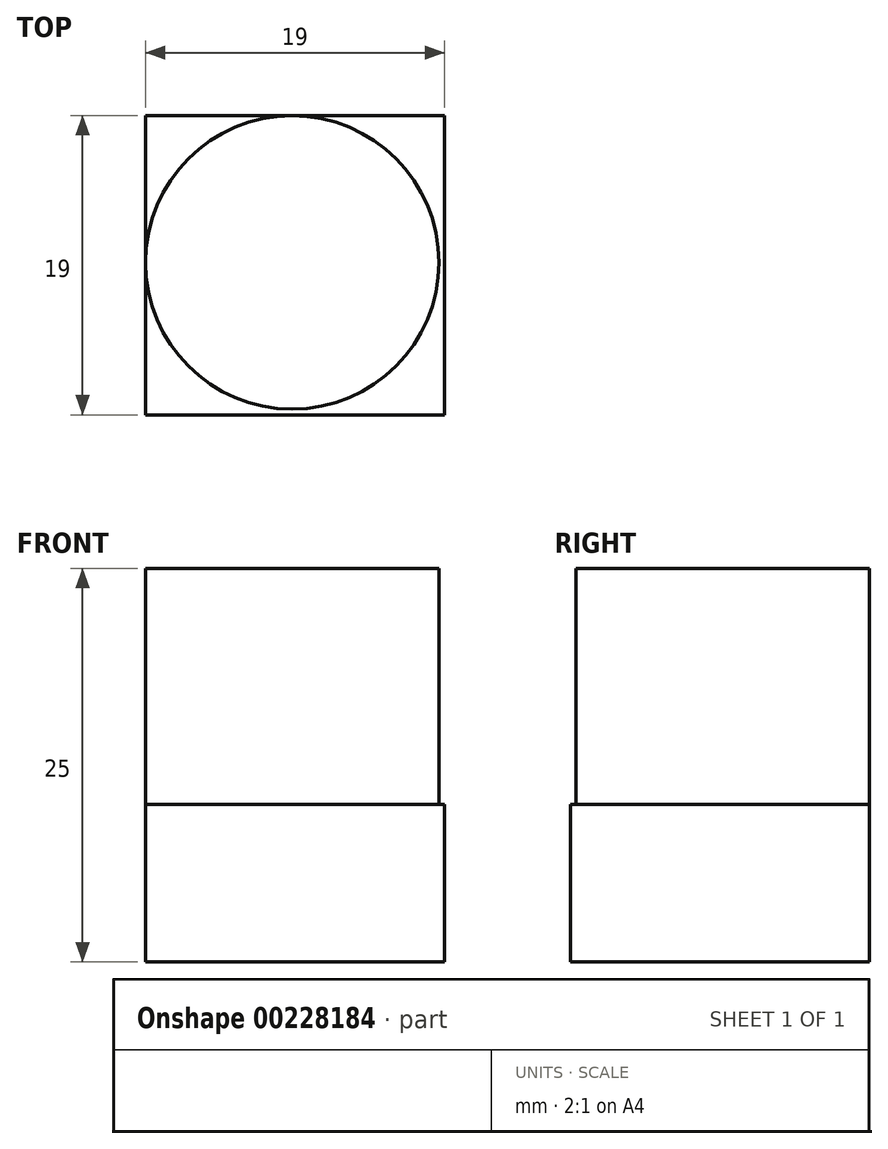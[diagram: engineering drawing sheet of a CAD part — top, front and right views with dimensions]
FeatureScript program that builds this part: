
annotation { "Feature Type Name" : "Feature", "Feature Type Description" : "" }
export const myFeature = defineFeature(function(context is Context, id is Id, definition is map)
    precondition{}
    {
        {
            var Q0;
            Q0=qCreatedBy(makeId("Top.planeOp"),FACE);
            var sketch = newSketch(context, id + "F0", { "sketchPlane" : qUnion([Q0])});
            skLineSegment(sketch, "E0.bottom", {"start": v(-9.32, 5.92) * mm, "end": v(9.68, 5.92) * mm});
            skLineSegment(sketch, "E0.top", {"start": v(-9.32, -13.08) * mm, "end": v(9.68, -13.08) * mm});
            skLineSegment(sketch, "E0.left", {"start": v(-9.32, 5.92) * mm, "end": v(-9.32, -13.08) * mm});
            skLineSegment(sketch, "E0.right", {"start": v(9.68, 5.92) * mm, "end": v(9.68, -13.08) * mm});
            skSolve(sketch);
        }
        {
            var Q0;
            Q0 = qSketchRegion(id + "F0", true);
            extrude(context, id + "F1", {"entities" : qUnion([Q0]), "depth" : 10 * mm});
        }
        {
            var Q0;
            Q0=makeQuery(id+"F1.opExtrude","CAP_FACE",FACE,{"disambiguationData":[OSD([sQuery(id+"F0.wireOp",EDGE,"E0.bottom"),sQuery(id+"F0.wireOp",EDGE,"E0.top"),sQuery(id+"F0.wireOp",EDGE,"E0.left"),sQuery(id+"F0.wireOp",EDGE,"E0.right")])],"isStart":false});
            var sketch = newSketch(context, id + "F2", { "sketchPlane" : qUnion([Q0])});
            skLineSegment(sketch, "E1", {"start": v(-9.32, 5.92) * mm, "end": v(9.68, -13.08) * mm, "construction": true});
            skCircle(sketch, "E2", {"center": v(0, -3.4) * mm, "radius": 9.32 * mm});
            skSolve(sketch);
        }
        {
            var Q0;
            Q0 = qSketchRegion(id + "F2", true);
            extrude(context, id + "F3", {"entities" : qUnion([Q0]), "operationType" : NewBodyOperationType.ADD, "depth" : 15 * mm});
        }
    });
